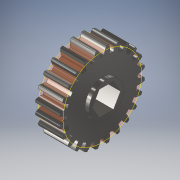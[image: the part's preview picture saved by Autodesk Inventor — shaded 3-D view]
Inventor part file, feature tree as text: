
AUTODESK INVENTOR PART (.ipt)
format: ipt  version: 2018 (Build 220112000, 112)  size: 232,448 bytes
history: native  units: in
note: dims shown in document units (in); Inventor stores cm internally (conversion verified against a paired STEP export)
features: other x3, sketch x1
ambient origin geometry x8: Origin, YZ Plane, XZ Plane, XY Plane, X Axis, Y Axis, Z Axis, Center Point
bodies: Solid1 (feature_tree)
feature tree (4):
  sketch  "Sketch1"  dims[d0=1.2in d1=1.0in d2=0.0in]
  other  "Srf1"
  other  "Bore"
  other  "pitch circle"
